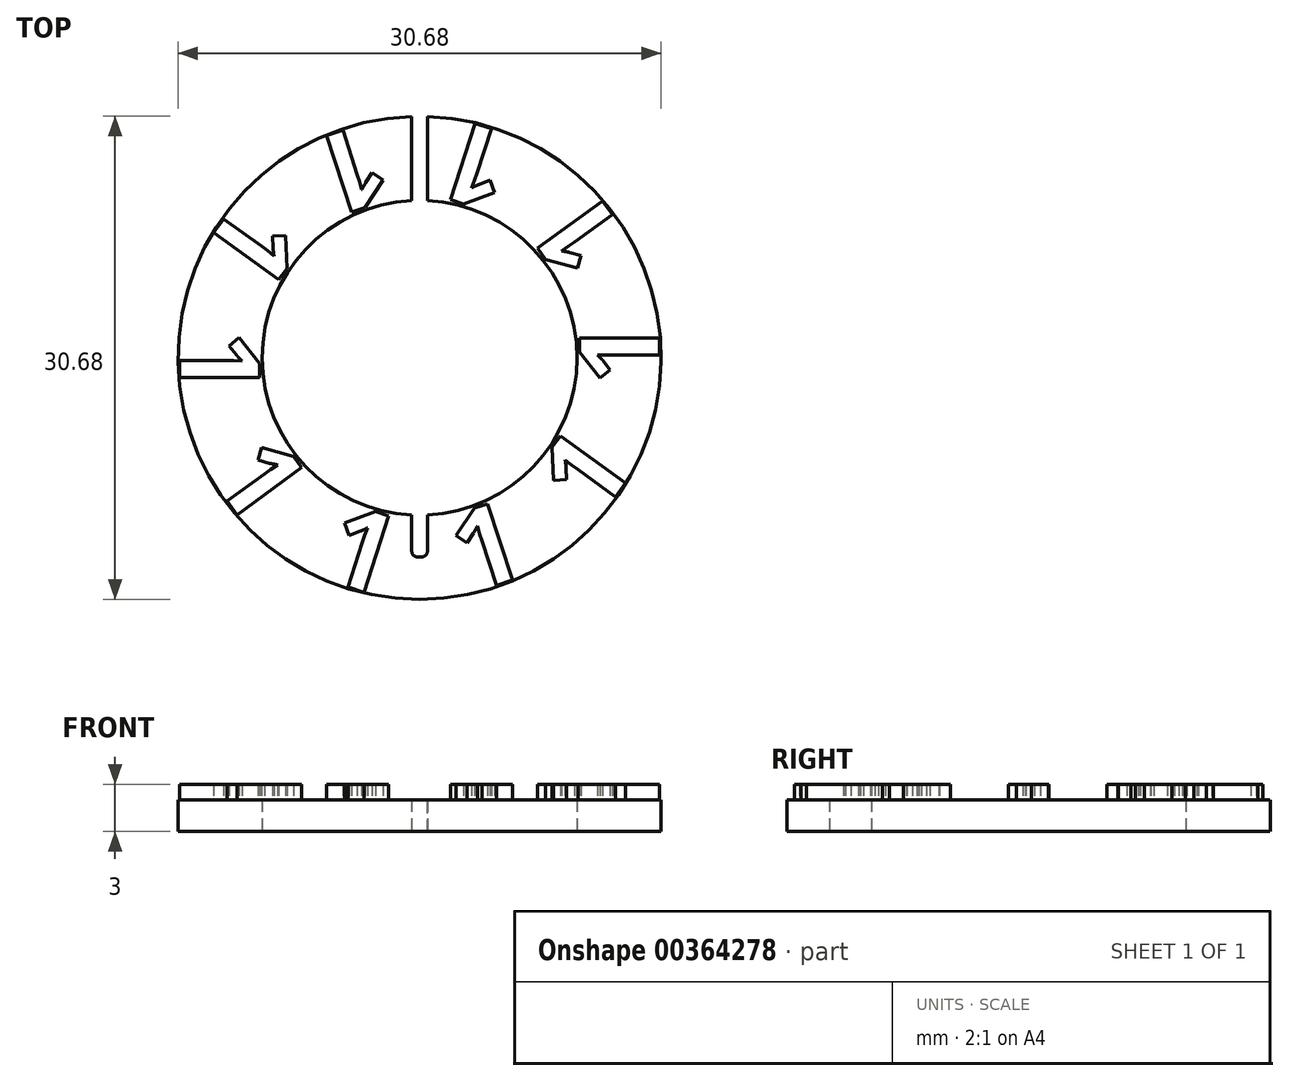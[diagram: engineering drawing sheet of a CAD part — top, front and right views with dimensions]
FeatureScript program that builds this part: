
annotation { "Feature Type Name" : "Feature", "Feature Type Description" : "" }
export const myFeature = defineFeature(function(context is Context, id is Id, definition is map)
    precondition{}
    {
        {
            var Q0;
            Q0=qCreatedBy(makeId("Top.planeOp"),FACE);
            var sketch = newSketch(context, id + "F0", { "sketchPlane" : qUnion([Q0])});
            skCircle(sketch, "E0", {"center": v(0, 0) * mm, "radius": 10 * mm});
            skCircle(sketch, "E1", {"center": v(0, 0) * mm, "radius": 15.34 * mm});
            skLineSegment(sketch, "E2", {"start": v(-16.5, 15.34) * mm, "end": v(25.55, 15.34) * mm, "construction": true});
            skSolve(sketch);
        }
        {
            var Q0;
            Q0 = qSketchRegion(id + "F0", true);
            extrude(context, id + "F1", {"entities" : qUnion([Q0]), "depth" : 2 * mm});
        }
        {
            var Q0;
            Q0=makeQuery(id+"F1.opExtrude","CAP_FACE",FACE,{"disambiguationData":[OSD([sQuery(id+"F0.wireOp",EDGE,"E0"),sQuery(id+"F0.wireOp",EDGE,"E1")])],"isStart":false});
            var sketch = newSketch(context, id + "F2", { "sketchPlane" : qUnion([Q0])});
            skLineSegment(sketch, "E3.0", {"start": v(-16.5, 15.34) * mm, "end": v(25.55, 15.34) * mm, "construction": true});
            skSolve(sketch);
        }
        {
            var Q0;
            Q0=sQuery(id+"F0.wireOp",EDGE,"E2");
            var Q1;
            Q1=sQuery(id+"F2.wireOp",EDGE,"E3.0");
            cPlane(context, id + "F3", {"entities" : qUnion([Q0, Q1]), "cplaneType" : CPlaneType.LINE_ANGLE, "offset" : 25 * mm, "angle" : 0 * degree, "width" : 150 * mm, "height" : 150 * mm});
        }
        {
            var Q0;
            Q0=qCreatedBy(id+"F3.planeOp",FACE);
            var sketch = newSketch(context, id + "F4", { "sketchPlane" : qUnion([Q0])});
            skLineSegment(sketch, "E4.0", {"start": v(-16.5, 2) * mm, "end": v(25.55, 2) * mm, "construction": true});
            skLineSegment(sketch, "E4.1", {"start": v(-16.5, 0) * mm, "end": v(25.55, 0) * mm, "construction": true});
            skLineSegment(sketch, "E5.bottom", {"start": v(0.5, 2) * mm, "end": v(-0.5, 2) * mm});
            skLineSegment(sketch, "E5.top", {"start": v(0.5, 0) * mm, "end": v(-0.5, 0) * mm});
            skLineSegment(sketch, "E5.left", {"start": v(0.5, 2) * mm, "end": v(0.5, 0) * mm});
            skLineSegment(sketch, "E5.right", {"start": v(-0.5, 2) * mm, "end": v(-0.5, 0) * mm});
            skSolve(sketch);
        }
        {
            var Q0;
            Q0=makeQuery(id+"F4.imprint","IMPRINT",FACE,{"disambiguationData":[TD([[makeQuery(id+"F4.imprint","IMPRINT",EDGE,{"derivedFrom":sQuery(id+"F4.wireOp",EDGE,"E5.bottom")}),1.0]])]});
            extrude(context, id + "F5", {"entities" : qUnion([Q0]), "operationType" : NewBodyOperationType.REMOVE, "depth" : 28 * mm});
        }
        {
            var Q0;
            Q0=makeQuery(id+"F5.boolean.opBoolean","COPY",EDGE,{"derivedFrom":makeQuery(id+"F5.opExtrude","CAP_EDGE",EDGE,{"disambiguationData":[OSD([sQuery(id+"F4.wireOp",EDGE,"E5.left")])],"isStart":false})});
            var Q1;
            Q1=makeQuery(id+"F5.boolean.opBoolean","COPY",EDGE,{"derivedFrom":makeQuery(id+"F5.opExtrude","CAP_EDGE",EDGE,{"disambiguationData":[OSD([sQuery(id+"F4.wireOp",EDGE,"E5.right")])],"isStart":false})});
            fillet(context, id + "F6", {"entities" : qUnion([Q0, Q1]), "radius" : 0.4 * mm, "tangentPropagation" : true, "allowEdgeOverflow" : false});
        }
        {
            var Q0;
            Q0=makeQuery(id+"F2.imprint","IMPRINT",FACE,{"disambiguationData":[TD([[makeQuery(id+"F2.imprint","IMPRINT",EDGE,{"derivedFrom":makeQuery(id+"F1.opExtrude","CAP_EDGE",EDGE,{"disambiguationData":[OSD([sQuery(id+"F0.wireOp",EDGE,"E0")])],"isStart":false})}),-1.0]])]});
            var sketch = newSketch(context, id + "F7", { "sketchPlane" : qUnion([Q0])});
            skPoint(sketch, "E6.0", {"position": v(0.5, 12.66) * mm});
            skCircle(sketch, "E7", {"center": v(0, 0) * mm, "radius": 12.67 * mm, "construction": true});
            skText(sketch, "E8", { "text": "1", "fontName": "OpenSans-Bold.ttf"});
            skLineSegment(sketch, "E9.0", {"start": v(-12.67, -4.12) * mm, "end": v(-12.67, 4.12) * mm, "construction": true});
            skLineSegment(sketch, "E9.1", {"start": v(-12.67, 4.12) * mm, "end": v(-7.83, 10.78) * mm, "construction": true});
            skLineSegment(sketch, "E9.2", {"start": v(-7.83, 10.78) * mm, "end": v(0, 13.33) * mm, "construction": true});
            skLineSegment(sketch, "E9.3", {"start": v(0, 13.33) * mm, "end": v(7.83, 10.78) * mm, "construction": true});
            skLineSegment(sketch, "E9.4", {"start": v(7.83, 10.78) * mm, "end": v(12.67, 4.12) * mm, "construction": true});
            skLineSegment(sketch, "E9.5", {"start": v(12.67, 4.12) * mm, "end": v(12.67, -4.12) * mm, "construction": true});
            skLineSegment(sketch, "E9.6", {"start": v(12.67, -4.12) * mm, "end": v(7.83, -10.78) * mm, "construction": true});
            skLineSegment(sketch, "E9.7", {"start": v(7.83, -10.78) * mm, "end": v(0, -13.33) * mm, "construction": true});
            skLineSegment(sketch, "E9.8", {"start": v(0, -13.33) * mm, "end": v(-7.83, -10.78) * mm, "construction": true});
            skLineSegment(sketch, "E9.9", {"start": v(-7.83, -10.78) * mm, "end": v(-12.67, -4.12) * mm, "construction": true});
            skPoint(sketch, "E9.0.midPoint", {"position": v(-12.67, 0) * mm});
            skPoint(sketch, "E10", {"position": v(-3.92, 12.05) * mm});
            const initialGuessF7  = {"E8": [-0.00309, 0.01503, -0.95106, -0.30902, 0.00514]};
            skSetInitialGuess(sketch, initialGuessF7);
            skSolve(sketch);
        }
        {
            var Q0;
            Q0=makeQuery(id+"F7.imprint","IMPRINT",FACE,{"disambiguationData":[TD([[makeQuery(id+"F7.imprint","IMPRINT",EDGE,{"derivedFrom":sQuery(id+"F7.wireOp",EDGE,"E8.sketch_text.stroke-0")}),-1.0]])]});
            extrude(context, id + "F8", {"entities" : qUnion([Q0]), "depth" : 1 * mm});
        }
        {
            var Q0;
            Q0=makeQuery(id+"F8.opExtrude","SWEPT_BODY",BODY,{"disambiguationData":[OSD([sQuery(id+"F7.wireOp",EDGE,"E8.sketch_text.stroke-0"),sQuery(id+"F7.wireOp",EDGE,"E8.sketch_text.stroke-1"),sQuery(id+"F7.wireOp",EDGE,"E8.sketch_text.stroke-2"),sQuery(id+"F7.wireOp",EDGE,"E8.sketch_text.stroke-3"),sQuery(id+"F7.wireOp",EDGE,"E8.sketch_text.stroke-4"),sQuery(id+"F7.wireOp",EDGE,"E8.sketch_text.stroke-5"),sQuery(id+"F7.wireOp",EDGE,"E8.sketch_text.stroke-6"),sQuery(id+"F7.wireOp",EDGE,"E8.sketch_text.stroke-7"),sQuery(id+"F7.wireOp",EDGE,"E8.sketch_text.stroke-8"),sQuery(id+"F7.wireOp",EDGE,"E8.sketch_text.stroke-9")])]});
            var Q1;
            Q1=sQuery(id+"F0.wireOp",EDGE,"E0");
            circularPattern(context, id + "F9", {"entities" : qUnion([Q0]), "axis" : qUnion([Q1]), "angle" : 360 * degree, "instanceCount" : 10, "equalSpace" : true});
        }
    });
